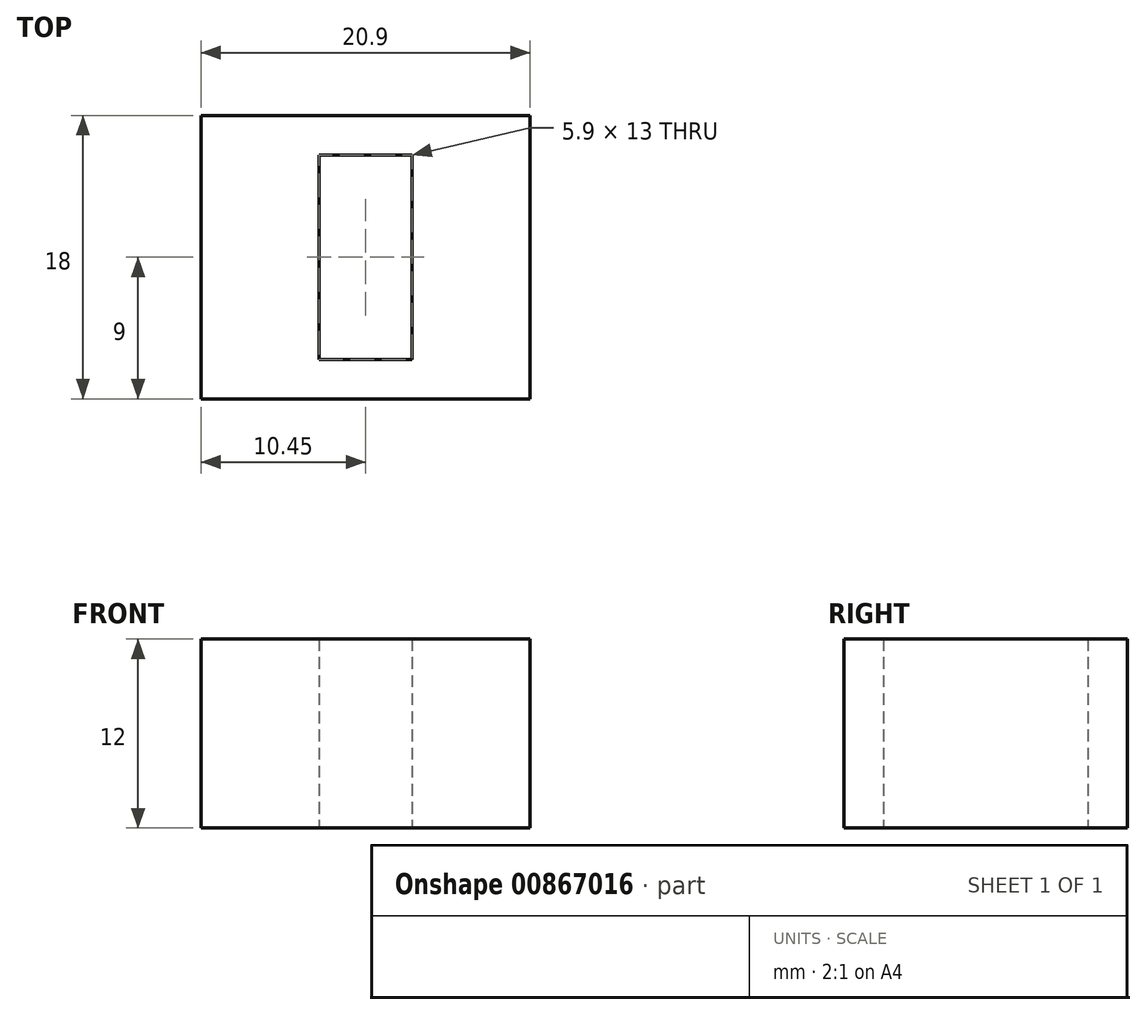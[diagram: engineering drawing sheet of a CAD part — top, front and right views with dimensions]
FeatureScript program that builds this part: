
annotation { "Feature Type Name" : "Feature", "Feature Type Description" : "" }
export const myFeature = defineFeature(function(context is Context, id is Id, definition is map)
    precondition{}
    {
        {
            var Q0;
            Q0=qCreatedBy(makeId("Top.planeOp"),FACE);
            var sketch = newSketch(context, id + "F0", { "sketchPlane" : qUnion([Q0])});
            skLineSegment(sketch, "E0.bottom", {"start": v(-10.45, 9) * mm, "end": v(10.45, 9) * mm});
            skLineSegment(sketch, "E0.top", {"start": v(-10.45, -9) * mm, "end": v(10.45, -9) * mm});
            skLineSegment(sketch, "E0.left", {"start": v(-10.45, 9) * mm, "end": v(-10.45, -9) * mm});
            skLineSegment(sketch, "E0.right", {"start": v(10.45, 9) * mm, "end": v(10.45, -9) * mm});
            skPoint(sketch, "E0.middle", {"position": v(0, 0) * mm});
            skLineSegment(sketch, "E1.bottom", {"start": v(-2.95, -6.5) * mm, "end": v(2.95, -6.5) * mm});
            skLineSegment(sketch, "E1.top", {"start": v(-2.95, 6.5) * mm, "end": v(2.95, 6.5) * mm});
            skLineSegment(sketch, "E1.left", {"start": v(-2.95, -6.5) * mm, "end": v(-2.95, 6.5) * mm});
            skLineSegment(sketch, "E1.right", {"start": v(2.95, -6.5) * mm, "end": v(2.95, 6.5) * mm});
            skSolve(sketch);
        }
        {
            var Q0;
            Q0 = qSketchRegion(id + "F0", true);
            extrude(context, id + "F1", {"entities" : qUnion([Q0]), "depth" : 12 * mm, "offsetDistance" : 25 * mm});
        }
    });
